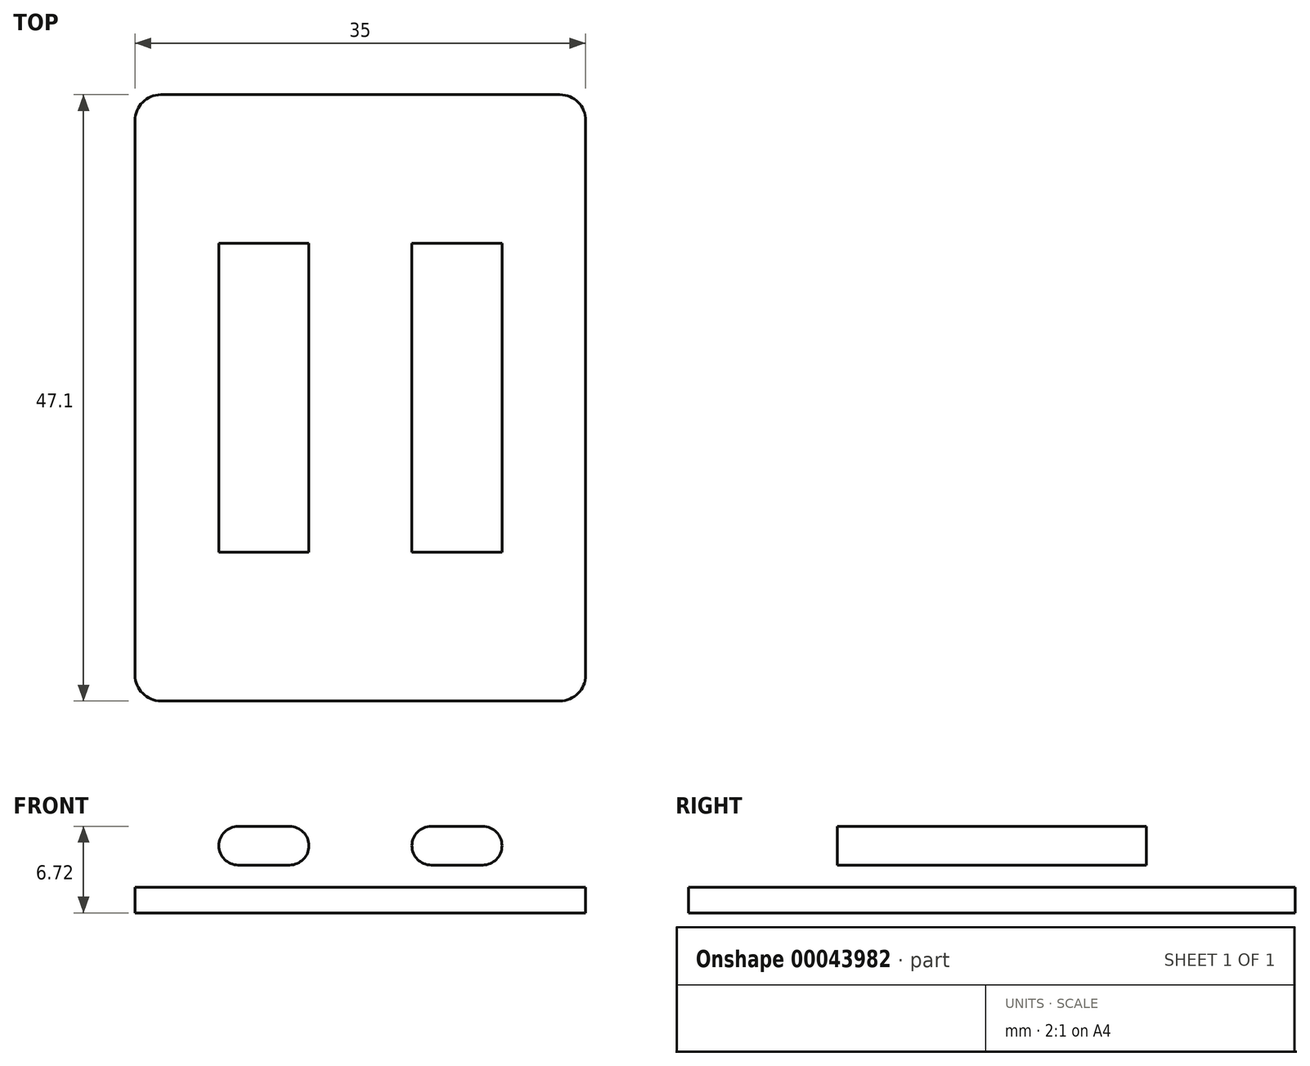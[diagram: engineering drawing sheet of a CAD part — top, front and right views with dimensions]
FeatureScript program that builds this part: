
annotation { "Feature Type Name" : "Feature", "Feature Type Description" : "" }
export const myFeature = defineFeature(function(context is Context, id is Id, definition is map)
    precondition{}
    {
        {
            var Q0;
            Q0=qCreatedBy(makeId("Top.planeOp"),FACE);
            var sketch = newSketch(context, id + "F0", { "sketchPlane" : qUnion([Q0])});
            skLineSegment(sketch, "E0.bottom", {"start": v(0, 0) * mm, "end": v(35, 0) * mm});
            skLineSegment(sketch, "E0.top", {"start": v(0, 47.1) * mm, "end": v(35, 47.1) * mm});
            skLineSegment(sketch, "E0.left", {"start": v(0, 0) * mm, "end": v(0, 47.1) * mm});
            skLineSegment(sketch, "E0.right", {"start": v(35, 0) * mm, "end": v(35, 47.1) * mm});
            skSolve(sketch);
        }
        {
            var Q0;
            Q0=makeQuery(id+"F0.imprint","IMPRINT",FACE,{"disambiguationData":[TD([[makeQuery(id+"F0.imprint","IMPRINT",EDGE,{"derivedFrom":sQuery(id+"F0.wireOp",EDGE,"E0.bottom")}),1.0]])]});
            extrude(context, id + "F1", {"entities" : qUnion([Q0]), "depth" : 2 * mm});
        }
        {
            var Q0;
            Q0=makeQuery(id+"F1.opExtrude","CAP_FACE",FACE,{"disambiguationData":[OSD([sQuery(id+"F0.wireOp",EDGE,"E0.bottom"),sQuery(id+"F0.wireOp",EDGE,"E0.top"),sQuery(id+"F0.wireOp",EDGE,"E0.left"),sQuery(id+"F0.wireOp",EDGE,"E0.right")])],"isStart":false});
            var sketch = newSketch(context, id + "F2", { "sketchPlane" : qUnion([Q0])});
            skLineSegment(sketch, "E1.rect.bottom", {"start": v(30, 35.55) * mm, "end": v(5, 35.55) * mm});
            skLineSegment(sketch, "E1.rect.top", {"start": v(30, 11.55) * mm, "end": v(5, 11.55) * mm});
            skLineSegment(sketch, "E1.rect.left", {"start": v(30, 35.55) * mm, "end": v(30, 11.55) * mm});
            skLineSegment(sketch, "E1.rect.right", {"start": v(5, 35.55) * mm, "end": v(5, 11.55) * mm});
            skPoint(sketch, "E1.rect.middle", {"position": v(17.5, 23.55) * mm});
            skPoint(sketch, "E1.rect.middle.positionSnap0", {"position": v(0, 23.55) * mm});
            skPoint(sketch, "E1.rect.middle.positionSnap1", {"position": v(17.5, 0) * mm});
            skPoint(sketch, "E1.rect.centerSnap0", {"position": v(0, 23.55) * mm});
            skPoint(sketch, "E1.rect.centerSnap1", {"position": v(17.5, 0) * mm});
            skSolve(sketch);
        }
        {
            var Q0;
            Q0=makeQuery(id+"F2.imprint","IMPRINT",FACE,{"disambiguationData":[TD([[makeQuery(id+"F2.imprint","IMPRINT",EDGE,{"derivedFrom":sQuery(id+"F2.wireOp",EDGE,"E1.rect.bottom")}),1.0]])]});
            extrude(context, id + "F3", {"entities" : qUnion([Q0]), "operationType" : NewBodyOperationType.ADD, "depth" : 16 * mm});
        }
        {
            var Q0;
            Q0=makeQuery(id+"F3.opExtrude","SWEPT_FACE",FACE,{"disambiguationData":[OSD([sQuery(id+"F2.wireOp",EDGE,"E1.rect.left")])]});
            var sketch = newSketch(context, id + "F4", { "sketchPlane" : qUnion([Q0])});
            skCircle(sketch, "E2", {"center": v(23.55, 18) * mm, "radius": 11 * mm});
            skSolve(sketch);
        }
        {
            var Q0;
            {var subQ0=makeQuery(id+"F3.opExtrude","CAP_EDGE",EDGE,{"disambiguationData":[OSD([sQuery(id+"F2.wireOp",EDGE,"E1.rect.left")])],"isStart":false});var subQ1=sQuery(id+"F4.wireOp",EDGE,"E2");var subQ3=makeQuery(id+"F4.imprint","INTERSECT",VERTEX,{"disambiguationData":[OD(0.0)],"derivedFrom":[subQ0,subQ1]});Q0=makeQuery(id+"F4.imprint","IMPRINT",FACE,{"disambiguationData":[TD([[makeQuery(id+"F4.imprint","IMPRINT",EDGE,{"disambiguationData":[TD([[subQ3,1.0]])],"derivedFrom":subQ1}),1.0]])]});}
            extrude(context, id + "F5", {"entities" : qUnion([Q0]), "operationType" : NewBodyOperationType.REMOVE, "endBound" : BoundingType.THROUGH_ALL, "oppositeDirection" : true, "depth" : 25 * mm});
        }
        {
            var Q0;
            Q0=makeQuery(id+"F3.opExtrude","SWEPT_FACE",FACE,{"disambiguationData":[OSD([sQuery(id+"F2.wireOp",EDGE,"E1.rect.top")])]});
            var sketch = newSketch(context, id + "F6", { "sketchPlane" : qUnion([Q0])});
            skLineSegment(sketch, "E3", {"start": v(5, 5.22) * mm, "end": v(8, 5.22) * mm, "construction": true});
            skLineSegment(sketch, "E4", {"start": v(8, 5.22) * mm, "end": v(12, 5.22) * mm, "construction": true});
            skLineSegment(sketch, "E5", {"start": v(12, 5.22) * mm, "end": v(23, 5.22) * mm, "construction": true});
            skLineSegment(sketch, "E6", {"start": v(23, 5.22) * mm, "end": v(27, 5.22) * mm, "construction": true});
            skLineSegment(sketch, "E7", {"start": v(27, 5.22) * mm, "end": v(30, 5.22) * mm, "construction": true});
            skArc(sketch, "E8.0.startCap", {"start": v(8, 3.72) * mm, "mid": v(6.5, 5.22) * mm, "end": v(8, 6.72) * mm});
            skArc(sketch, "E8.0.endCap", {"start": v(12, 6.72) * mm, "mid": v(13.5, 5.22) * mm, "end": v(12, 3.72) * mm});
            skLineSegment(sketch, "E8.0.left", {"start": v(8, 6.72) * mm, "end": v(12, 6.72) * mm});
            skLineSegment(sketch, "E8.0.right", {"start": v(8, 3.72) * mm, "end": v(12, 3.72) * mm});
            skArc(sketch, "E8.1.startCap", {"start": v(23, 3.72) * mm, "mid": v(21.5, 5.22) * mm, "end": v(23, 6.72) * mm});
            skArc(sketch, "E8.1.endCap", {"start": v(27, 6.72) * mm, "mid": v(28.5, 5.22) * mm, "end": v(27, 3.72) * mm});
            skLineSegment(sketch, "E8.1.left", {"start": v(23, 6.72) * mm, "end": v(27, 6.72) * mm});
            skLineSegment(sketch, "E8.1.right", {"start": v(23, 3.72) * mm, "end": v(27, 3.72) * mm});
            skSolve(sketch);
        }
        {
            var Q0;
            Q0=makeQuery(id+"F6.imprint","IMPRINT",FACE,{"disambiguationData":[TD([[makeQuery(id+"F6.imprint","IMPRINT",EDGE,{"derivedFrom":sQuery(id+"F6.wireOp",EDGE,"E8.0.startCap")}),-1.0]])]});
            var Q1;
            Q1=makeQuery(id+"F6.imprint","IMPRINT",FACE,{"disambiguationData":[TD([[makeQuery(id+"F6.imprint","IMPRINT",EDGE,{"derivedFrom":sQuery(id+"F6.wireOp",EDGE,"E8.1.startCap")}),-1.0]])]});
            extrude(context, id + "F7", {"entities" : qUnion([Q0, Q1]), "operationType" : NewBodyOperationType.REMOVE, "endBound" : BoundingType.THROUGH_ALL, "oppositeDirection" : true, "depth" : 25 * mm});
        }
        {
            var Q0;
            Q0=makeQuery(id+"F7.boolean.opBoolean","COPY",EDGE,{"derivedFrom":makeQuery(id+"F7.opExtrude","CAP_EDGE",EDGE,{"disambiguationData":[OSD([sQuery(id+"F6.wireOp",EDGE,"E8.1.left")])],"isStart":true})});
            var Q1;
            Q1=makeQuery(id+"F7.boolean.opBoolean","COPY",EDGE,{"derivedFrom":makeQuery(id+"F7.opExtrude","CAP_EDGE",EDGE,{"disambiguationData":[OSD([sQuery(id+"F6.wireOp",EDGE,"E8.0.left")])],"isStart":true})});
            var Q2;
            Q2=makeQuery(id+"F7.boolean.opBoolean","INTERSECT",EDGE,{"derivedFrom":[makeQuery(id+"F3.opExtrude","SWEPT_FACE",FACE,{"disambiguationData":[OSD([sQuery(id+"F2.wireOp",EDGE,"E1.rect.bottom")])]}),makeQuery(id+"F7.opExtrude","SWEPT_FACE",FACE,{"disambiguationData":[OSD([sQuery(id+"F6.wireOp",EDGE,"E8.1.left")])]})]});
            var Q3;
            Q3=makeQuery(id+"F7.boolean.opBoolean","INTERSECT",EDGE,{"derivedFrom":[makeQuery(id+"F3.opExtrude","SWEPT_FACE",FACE,{"disambiguationData":[OSD([sQuery(id+"F2.wireOp",EDGE,"E1.rect.bottom")])]}),makeQuery(id+"F7.opExtrude","SWEPT_FACE",FACE,{"disambiguationData":[OSD([sQuery(id+"F6.wireOp",EDGE,"E8.0.left")])]})]});
            var Q4;
            Q4=makeQuery(id+"F1.opExtrude","SWEPT_EDGE",EDGE,{"disambiguationData":[OSD([sQuery(id+"F0.wireOp",EDGE,"E0.top"),sQuery(id+"F0.wireOp",EDGE,"E0.right")])]});
            var Q5;
            Q5=makeQuery(id+"F1.opExtrude","SWEPT_EDGE",EDGE,{"disambiguationData":[OSD([sQuery(id+"F0.wireOp",EDGE,"E0.top"),sQuery(id+"F0.wireOp",EDGE,"E0.left")])]});
            var Q6;
            Q6=makeQuery(id+"F1.opExtrude","SWEPT_EDGE",EDGE,{"disambiguationData":[OSD([sQuery(id+"F0.wireOp",EDGE,"E0.bottom"),sQuery(id+"F0.wireOp",EDGE,"E0.right")])]});
            var Q7;
            Q7=makeQuery(id+"F1.opExtrude","SWEPT_EDGE",EDGE,{"disambiguationData":[OSD([sQuery(id+"F0.wireOp",EDGE,"E0.bottom"),sQuery(id+"F0.wireOp",EDGE,"E0.left")])]});
            fillet(context, id + "F8", {"entities" : qUnion([Q0, Q1, Q2, Q3, Q4, Q5, Q6, Q7]), "radius" : 2 * mm, "tangentPropagation" : true, "allowEdgeOverflow" : false});
        }
    });
